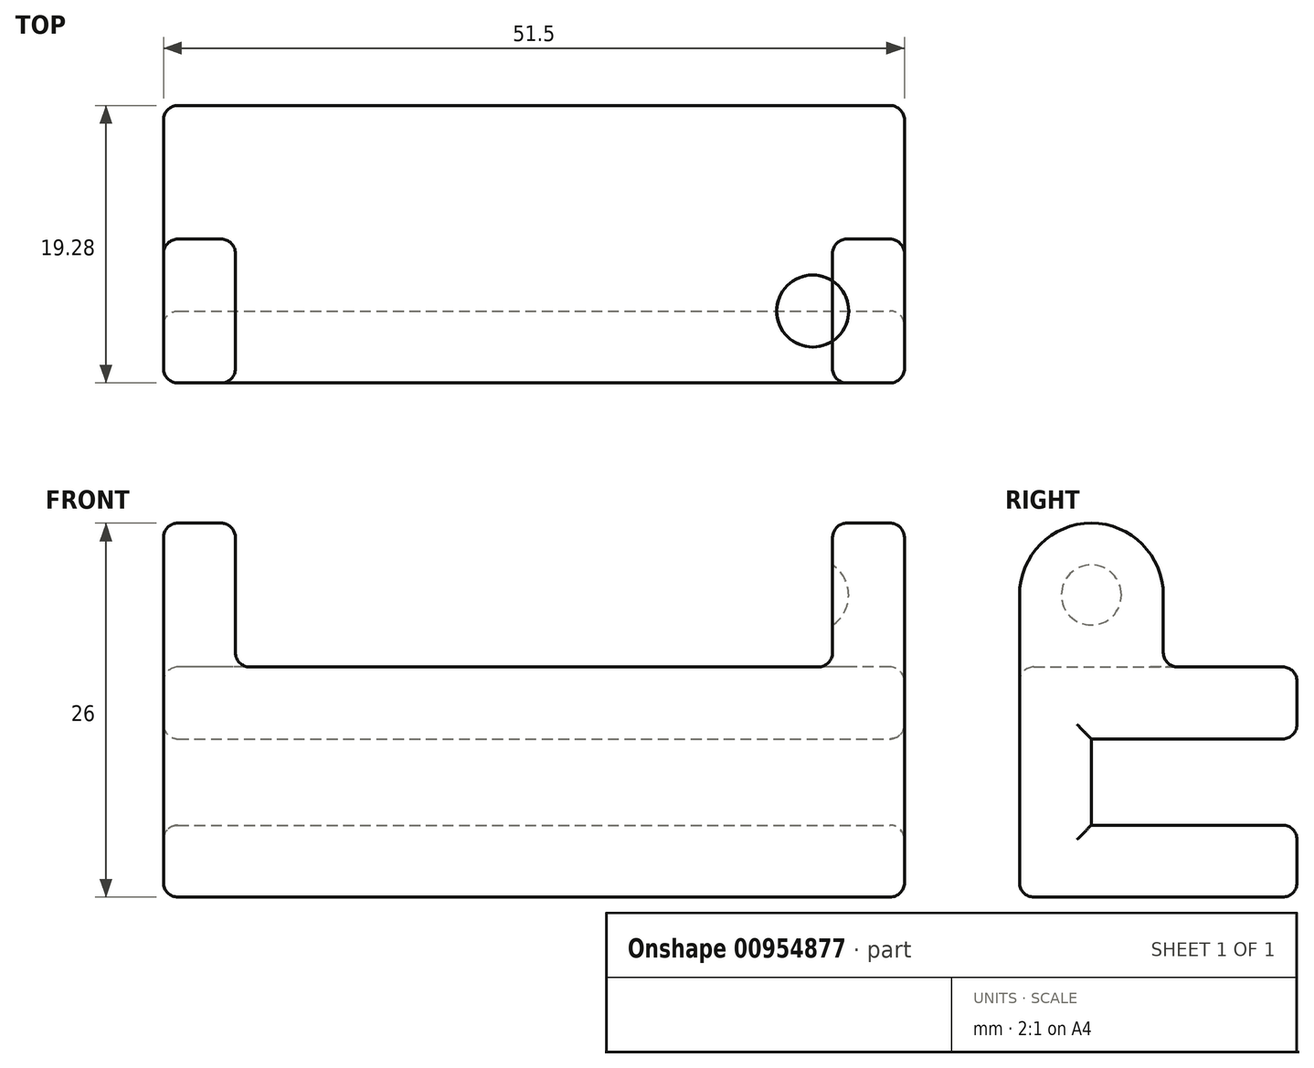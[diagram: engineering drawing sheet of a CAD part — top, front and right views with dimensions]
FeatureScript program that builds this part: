
annotation { "Feature Type Name" : "Feature", "Feature Type Description" : "" }
export const myFeature = defineFeature(function(context is Context, id is Id, definition is map)
    precondition{}
    {
        {
            var Q0;
            Q0=qCreatedBy(makeId("Top.planeOp"),FACE);
            var sketch = newSketch(context, id + "F0", { "sketchPlane" : qUnion([Q0])});
            skLineSegment(sketch, "E0.bottom", {"start": v(25.75, -9.64) * mm, "end": v(-25.75, -9.64) * mm});
            skLineSegment(sketch, "E0.top", {"start": v(25.75, 9.64) * mm, "end": v(-25.75, 9.64) * mm});
            skLineSegment(sketch, "E0.left", {"start": v(25.75, -9.64) * mm, "end": v(25.75, 9.64) * mm});
            skLineSegment(sketch, "E0.right", {"start": v(-25.75, -9.64) * mm, "end": v(-25.75, 9.64) * mm});
            skPoint(sketch, "E0.middle", {"position": v(0, 0) * mm});
            skSolve(sketch);
        }
        {
            var Q0;
            Q0 = qSketchRegion(id + "F0", true);
            extrude(context, id + "F1", {"entities" : qUnion([Q0]), "depth" : 8 * mm, "offsetDistance" : 25 * mm, "hasSecondDirection" : true, "secondDirectionOppositeDirection" : true, "secondDirectionDepth" : 8 * mm});
        }
        {
            var Q0;
            Q0=qCreatedBy(makeId("Right.planeOp"),FACE);
            var sketch = newSketch(context, id + "F2", { "sketchPlane" : qUnion([Q0])});
            skLineSegment(sketch, "E1.bottom", {"start": v(9.64, -3) * mm, "end": v(-4.64, -3) * mm});
            skLineSegment(sketch, "E1.top", {"start": v(9.64, 3) * mm, "end": v(-4.64, 3) * mm});
            skLineSegment(sketch, "E1.left", {"start": v(9.64, -3) * mm, "end": v(9.64, 3) * mm});
            skLineSegment(sketch, "E1.right", {"start": v(-4.64, -3) * mm, "end": v(-4.64, 3) * mm});
            skPoint(sketch, "E1.middle", {"position": v(2.5, 0) * mm});
            skSolve(sketch);
        }
        {
            var Q0;
            Q0 = qSketchRegion(id + "F2", true);
            extrude(context, id + "F3", {"entities" : qUnion([Q0]), "operationType" : NewBodyOperationType.REMOVE, "endBound" : BoundingType.THROUGH_ALL, "oppositeDirection" : true, "depth" : 25 * mm, "offsetDistance" : 25 * mm, "hasSecondDirection" : true, "secondDirectionBound" : SecondDirectionBoundingType.THROUGH_ALL, "secondDirectionOppositeDirection" : false, "secondDirectionDepth" : 25 * mm});
        }
        {
            var Q0;
            Q0=qCreatedBy(makeId("Right.planeOp"),FACE);
            var sketch = newSketch(context, id + "F4", { "sketchPlane" : qUnion([Q0])});
            skArc(sketch, "E2", {"start": v(0.36, 13) * mm, "mid": v(-4.64, 18) * mm, "end": v(-9.64, 13) * mm});
            skLineSegment(sketch, "E3.bottom", {"start": v(-9.64, 8) * mm, "end": v(0.36, 8) * mm});
            skLineSegment(sketch, "E3.left", {"start": v(-9.64, 8) * mm, "end": v(-9.64, 13) * mm});
            skLineSegment(sketch, "E3.right", {"start": v(0.36, 8) * mm, "end": v(0.36, 13) * mm});
            skSolve(sketch);
        }
        {
            var Q0;
            Q0=makeQuery(id+"F4.imprint","IMPRINT",FACE,{"disambiguationData":[TD([[makeQuery(id+"F4.imprint","IMPRINT",EDGE,{"derivedFrom":sQuery(id+"F4.wireOp",EDGE,"E2")}),1.0]])]});
            var Q1;
            Q1=makeQuery(id+"F1.opExtrude","SWEPT_FACE",FACE,{"disambiguationData":[OSD([sQuery(id+"F0.wireOp",EDGE,"E0.left")])]});
            var Q2;
            Q2=makeQuery(id+"F1.opExtrude","SWEPT_FACE",FACE,{"disambiguationData":[OSD([sQuery(id+"F0.wireOp",EDGE,"E0.right")])]});
            extrude(context, id + "F5", {"entities" : qUnion([Q0]), "operationType" : NewBodyOperationType.ADD, "endBound" : BoundingType.UP_TO_SURFACE, "depth" : 25 * mm, "endBoundEntityFace" : qUnion([Q1]), "offsetDistance" : 5 * mm, "offsetOppositeDirection" : true, "hasSecondDirection" : true, "secondDirectionBound" : SecondDirectionBoundingType.UP_TO_SURFACE, "secondDirectionOppositeDirection" : true, "secondDirectionDepth" : 25 * mm, "secondDirectionBoundEntityFace" : qUnion([Q2])});
        }
        {
            var Q0;
            Q0 = qSketchRegion(id + "F4", true);
            extrude(context, id + "F6", {"entities" : qUnion([Q0]), "operationType" : NewBodyOperationType.REMOVE, "oppositeDirection" : true, "depth" : (20.12 + .625) * mm, "offsetDistance" : 25 * mm, "hasSecondDirection" : true, "secondDirectionOppositeDirection" : false, "secondDirectionDepth" : (20.12 + .625) * mm});
        }
        {
            var Q0;
            Q0=makeQuery(id+"F5.boolean.opBoolean","MERGE",FACE,{"derivedFrom":[makeQuery(id+"F1.opExtrude","SWEPT_FACE",FACE,{"disambiguationData":[OSD([sQuery(id+"F0.wireOp",EDGE,"E0.bottom")])]}),makeQuery(id+"F5.opExtrude","SWEPT_FACE",FACE,{"disambiguationData":[OSD([sQuery(id+"F4.wireOp",EDGE,"E3.left")])]})]});
            cPlane(context, id + "F7", {"entities" : qUnion([Q0]), "cplaneType" : CPlaneType.OFFSET, "offset" : 5 * mm, "oppositeDirection" : true, "width" : 150 * mm, "height" : 150 * mm});
        }
        {
            var Q0;
            Q0=qCreatedBy(id+"F7.planeOp",FACE);
            var sketch = newSketch(context, id + "F8", { "sketchPlane" : qUnion([Q0])});
            skLineSegment(sketch, "E4", {"start": v(19.38, 15.5) * mm, "end": v(19.38, 10.5) * mm});
            skArc(sketch, "E5", {"start": v(19.37, 10.5) * mm, "mid": v(21.88, 13) * mm, "end": v(19.37, 15.5) * mm});
            skSolve(sketch);
        }
        {
            var Q0;
            Q0 = qSketchRegion(id + "F8", true);
            var Q1;
            Q1=sQuery(id+"F8.wireOp",EDGE,"E4");
            revolve(context, id + "F9", {"operationType" : NewBodyOperationType.REMOVE, "surfaceOperationType" : NewSurfaceOperationType.NEW, "entities" : qUnion([Q0]), "axis" : qUnion([Q1]), "revolveType" : RevolveType.FULL, "oppositeDirection" : true});
        }
        {
            var Q0;
            Q0=makeQuery(id+"F6.boolean.opBoolean","MERGE",FACE,{"derivedFrom":[makeQuery(id+"F1.opExtrude","CAP_FACE",FACE,{"disambiguationData":[OSD([sQuery(id+"F0.wireOp",EDGE,"E0.bottom"),sQuery(id+"F0.wireOp",EDGE,"E0.top"),sQuery(id+"F0.wireOp",EDGE,"E0.left"),sQuery(id+"F0.wireOp",EDGE,"E0.right")])],"isStart":false})],"fromTools":[makeQuery(id+"F6.opExtrude","SWEPT_FACE",FACE,{"disambiguationData":[OSD([sQuery(id+"F4.wireOp",EDGE,"E3.bottom")])]})]});
            var Q1;
            Q1=makeQuery(id+"F5.boolean.opBoolean","MERGE",FACE,{"derivedFrom":[makeQuery(id+"F1.opExtrude","SWEPT_FACE",FACE,{"disambiguationData":[OSD([sQuery(id+"F0.wireOp",EDGE,"E0.bottom")])]}),makeQuery(id+"F5.opExtrude","SWEPT_FACE",FACE,{"disambiguationData":[OSD([sQuery(id+"F4.wireOp",EDGE,"E3.left")])]})]});
            var Q2;
            Q2=makeQuery(id+"F5.boolean.opBoolean","MERGE",FACE,{"derivedFrom":[makeQuery(id+"F1.opExtrude","SWEPT_FACE",FACE,{"disambiguationData":[OSD([sQuery(id+"F0.wireOp",EDGE,"E0.left")])]}),makeQuery(id+"F5.opExtrude","CAP_FACE",FACE,{"disambiguationData":[OSD([sQuery(id+"F4.wireOp",EDGE,"E2"),sQuery(id+"F4.wireOp",EDGE,"E3.bottom"),sQuery(id+"F4.wireOp",EDGE,"E3.left"),sQuery(id+"F4.wireOp",EDGE,"E3.right")])],"isStart":false})]});
            var Q3;
            Q3=makeQuery(id+"F5.boolean.opBoolean","MERGE",FACE,{"derivedFrom":[makeQuery(id+"F1.opExtrude","SWEPT_FACE",FACE,{"disambiguationData":[OSD([sQuery(id+"F0.wireOp",EDGE,"E0.right")])]}),makeQuery(id+"F5.opExtrude","CAP_FACE",FACE,{"disambiguationData":[OSD([sQuery(id+"F4.wireOp",EDGE,"E2"),sQuery(id+"F4.wireOp",EDGE,"E3.bottom"),sQuery(id+"F4.wireOp",EDGE,"E3.left"),sQuery(id+"F4.wireOp",EDGE,"E3.right")])],"isStart":true})]});
            var Q4;
            Q4=makeQuery(id+"F1.opExtrude","CAP_FACE",FACE,{"disambiguationData":[OSD([sQuery(id+"F0.wireOp",EDGE,"E0.bottom"),sQuery(id+"F0.wireOp",EDGE,"E0.top"),sQuery(id+"F0.wireOp",EDGE,"E0.left"),sQuery(id+"F0.wireOp",EDGE,"E0.right")])],"isStart":true});
            var Q5;
            {var subQ2=sQuery(id+"F0.wireOp",EDGE,"E0.top");Q5=makeQuery(id+"F3.boolean.opBoolean","SPLIT",FACE,{"disambiguationData":[TD([makeQuery(id+"F3.opExtrude","SWEPT_FACE",FACE,{"disambiguationData":[OSD([sQuery(id+"F2.wireOp",EDGE,"E1.top")])]})])],"derivedFrom":makeQuery(id+"F1.opExtrude","SWEPT_FACE",FACE,{"disambiguationData":[OSD([subQ2])]})});}
            var Q6;
            {var subQ2=sQuery(id+"F0.wireOp",EDGE,"E0.top");Q6=makeQuery(id+"F3.boolean.opBoolean","SPLIT",FACE,{"disambiguationData":[TD([makeQuery(id+"F3.opExtrude","SWEPT_FACE",FACE,{"disambiguationData":[OSD([sQuery(id+"F2.wireOp",EDGE,"E1.bottom")])]})])],"derivedFrom":makeQuery(id+"F1.opExtrude","SWEPT_FACE",FACE,{"disambiguationData":[OSD([subQ2])]})});}
            fillet(context, id + "F10", {"entities" : qUnion([Q0, Q1, Q2, Q3, Q4, Q5, Q6]), "radius" : 1 * mm, "tangentPropagation" : true, "allowEdgeOverflow" : false});
        }
    });
